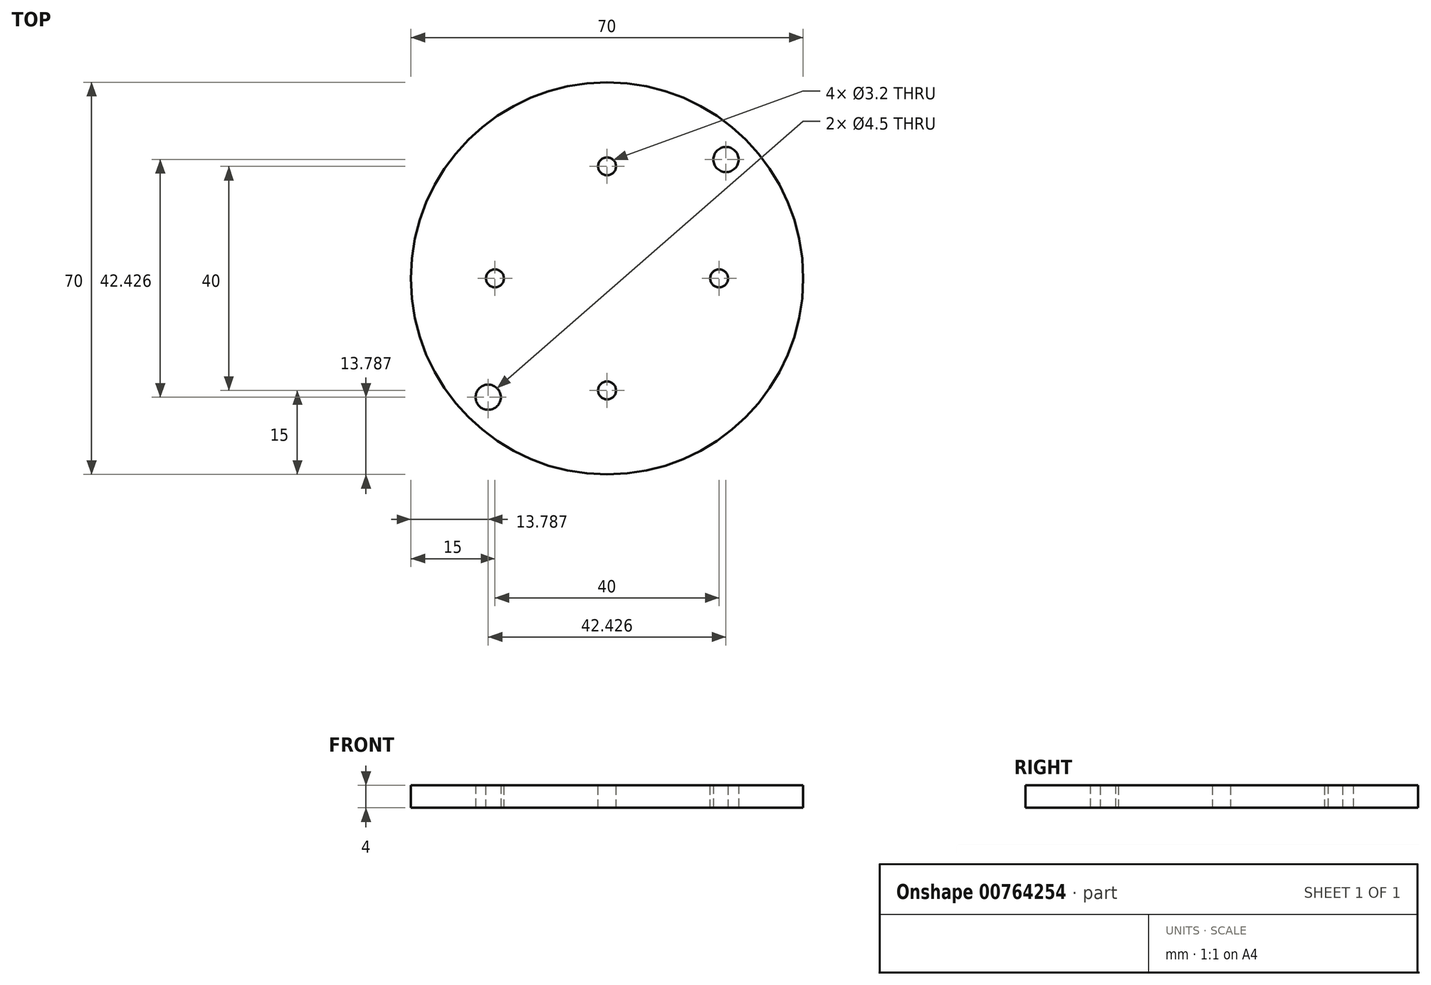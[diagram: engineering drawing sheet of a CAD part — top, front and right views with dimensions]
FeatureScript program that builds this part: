
annotation { "Feature Type Name" : "Feature", "Feature Type Description" : "" }
export const myFeature = defineFeature(function(context is Context, id is Id, definition is map)
    precondition{}
    {
        {
            var Q0;
            Q0=qCreatedBy(makeId("Top.planeOp"),FACE);
            var sketch = newSketch(context, id + "F0", { "sketchPlane" : qUnion([Q0])});
            skCircle(sketch, "E0", {"center": v(0, 0) * mm, "radius": 35 * mm});
            skLineSegment(sketch, "E1", {"start": v(-21.21, -21.21) * mm, "end": v(0, 0) * mm});
            skLineSegment(sketch, "E2", {"start": v(0, 0) * mm, "end": v(21.21, 21.21) * mm});
            skLineSegment(sketch, "E3", {"start": v(21.21, 21.21) * mm, "end": v(0, 0) * mm});
            skCircle(sketch, "E4", {"center": v(21.21, 21.21) * mm, "radius": 2.25 * mm});
            skCircle(sketch, "E5", {"center": v(-21.21, -21.21) * mm, "radius": 2.25 * mm});
            skSolve(sketch);
        }
        {
            var Q0;
            Q0 = qSketchRegion(id + "F0", true);
            extrude(context, id + "F1", {"entities" : qUnion([Q0]), "depth" : 4 * mm, "offsetDistance" : 25 * mm});
        }
        {
            var Q0;
            Q0=makeQuery(id+"F1.opExtrude","CAP_FACE",FACE,{"disambiguationData":[OSD([sQuery(id+"F0.wireOp",EDGE,"E0"),sQuery(id+"F0.wireOp",EDGE,"de1Grw44-cGFu-5i0o-8A4r-Zq54lEinxhuE"),sQuery(id+"F0.wireOp",EDGE,"E4"),sQuery(id+"F0.wireOp",EDGE,"CMPWbkWI-gggi-udjs-4O77-vAyiC2Vh54Nz"),sQuery(id+"F0.wireOp",EDGE,"E5")])],"isStart":false});
            var sketch = newSketch(context, id + "F2", { "sketchPlane" : qUnion([Q0])});
            skCircle(sketch, "E6", {"center": v(0, 0) * mm, "radius": 20 * mm});
            skCircle(sketch, "E7", {"center": v(0, -20) * mm, "radius": 1.6 * mm});
            skCircle(sketch, "E8", {"center": v(20, 0) * mm, "radius": 1.6 * mm});
            skCircle(sketch, "E9", {"center": v(0, 20) * mm, "radius": 1.6 * mm});
            skCircle(sketch, "E10", {"center": v(-20, 0) * mm, "radius": 1.6 * mm});
            skLineSegment(sketch, "E11", {"start": v(0, 0) * mm, "end": v(0, 20) * mm});
            skLineSegment(sketch, "E12", {"start": v(-20, 0) * mm, "end": v(0, 0) * mm});
            skLineSegment(sketch, "E13", {"start": v(0, -20) * mm, "end": v(0, 0) * mm});
            skLineSegment(sketch, "E14", {"start": v(0, 0) * mm, "end": v(20, 0) * mm});
            skSolve(sketch);
        }
        {
            var Q0;
            {var subQ0=sQuery(id+"F2.wireOp",EDGE,"E6");var subQ1=makeQuery(id+"F2.imprint","INTERSECT",VERTEX,{"derivedFrom":[subQ0,sQuery(id+"F2.wireOp",EDGE,"E11")]});Q0=makeQuery(id+"F2.imprint","IMPRINT",FACE,{"disambiguationData":[TD([[makeQuery(id+"F2.imprint","IMPRINT",EDGE,{"disambiguationData":[TD([[subQ1,1.0]])],"derivedFrom":subQ0}),-1.0]])]});}
            var Q1;
            {var subQ0=sQuery(id+"F2.wireOp",EDGE,"E11");var subQ1=sQuery(id+"F2.wireOp",EDGE,"E6");var subQ2=makeQuery(id+"F2.imprint","INTERSECT",VERTEX,{"derivedFrom":[subQ1,subQ0]});Q1=makeQuery(id+"F2.imprint","IMPRINT",FACE,{"disambiguationData":[TD([[makeQuery(id+"F2.imprint","IMPRINT",EDGE,{"disambiguationData":[TD([[subQ2,1.0]])],"derivedFrom":subQ1}),1.0]])]});}
            var Q2;
            {var subQ0=sQuery(id+"F2.wireOp",EDGE,"E11");var subQ1=sQuery(id+"F2.wireOp",EDGE,"E6");var subQ2=makeQuery(id+"F2.imprint","INTERSECT",VERTEX,{"derivedFrom":[subQ1,subQ0]});Q2=makeQuery(id+"F2.imprint","IMPRINT",FACE,{"disambiguationData":[TD([[makeQuery(id+"F2.imprint","IMPRINT",EDGE,{"disambiguationData":[TD([[subQ2,-1.0]])],"derivedFrom":subQ1}),1.0]])]});}
            var Q3;
            {var subQ0=sQuery(id+"F2.wireOp",EDGE,"E6");var subQ1=makeQuery(id+"F2.imprint","INTERSECT",VERTEX,{"derivedFrom":[subQ0,sQuery(id+"F2.wireOp",EDGE,"E12")]});Q3=makeQuery(id+"F2.imprint","IMPRINT",FACE,{"disambiguationData":[TD([[makeQuery(id+"F2.imprint","IMPRINT",EDGE,{"disambiguationData":[TD([[subQ1,1.0]])],"derivedFrom":subQ0}),-1.0]])]});}
            var Q4;
            {var subQ0=sQuery(id+"F2.wireOp",EDGE,"E12");var subQ1=sQuery(id+"F2.wireOp",EDGE,"E6");var subQ2=makeQuery(id+"F2.imprint","INTERSECT",VERTEX,{"derivedFrom":[subQ1,subQ0]});Q4=makeQuery(id+"F2.imprint","IMPRINT",FACE,{"disambiguationData":[TD([[makeQuery(id+"F2.imprint","IMPRINT",EDGE,{"disambiguationData":[TD([[subQ2,1.0]])],"derivedFrom":subQ1}),1.0]])]});}
            var Q5;
            {var subQ0=sQuery(id+"F2.wireOp",EDGE,"E12");var subQ1=sQuery(id+"F2.wireOp",EDGE,"E6");var subQ2=makeQuery(id+"F2.imprint","INTERSECT",VERTEX,{"derivedFrom":[subQ1,subQ0]});Q5=makeQuery(id+"F2.imprint","IMPRINT",FACE,{"disambiguationData":[TD([[makeQuery(id+"F2.imprint","IMPRINT",EDGE,{"disambiguationData":[TD([[subQ2,-1.0]])],"derivedFrom":subQ1}),1.0]])]});}
            var Q6;
            {var subQ0=sQuery(id+"F2.wireOp",EDGE,"E6");var subQ1=makeQuery(id+"F2.imprint","INTERSECT",VERTEX,{"derivedFrom":[subQ0,sQuery(id+"F2.wireOp",EDGE,"E13")]});Q6=makeQuery(id+"F2.imprint","IMPRINT",FACE,{"disambiguationData":[TD([[makeQuery(id+"F2.imprint","IMPRINT",EDGE,{"disambiguationData":[TD([[subQ1,1.0]])],"derivedFrom":subQ0}),-1.0]])]});}
            var Q7;
            {var subQ0=sQuery(id+"F2.wireOp",EDGE,"E13");var subQ1=sQuery(id+"F2.wireOp",EDGE,"E6");var subQ2=makeQuery(id+"F2.imprint","INTERSECT",VERTEX,{"derivedFrom":[subQ1,subQ0]});Q7=makeQuery(id+"F2.imprint","IMPRINT",FACE,{"disambiguationData":[TD([[makeQuery(id+"F2.imprint","IMPRINT",EDGE,{"disambiguationData":[TD([[subQ2,1.0]])],"derivedFrom":subQ1}),1.0]])]});}
            var Q8;
            {var subQ0=sQuery(id+"F2.wireOp",EDGE,"E13");var subQ1=sQuery(id+"F2.wireOp",EDGE,"E6");var subQ2=makeQuery(id+"F2.imprint","INTERSECT",VERTEX,{"derivedFrom":[subQ1,subQ0]});Q8=makeQuery(id+"F2.imprint","IMPRINT",FACE,{"disambiguationData":[TD([[makeQuery(id+"F2.imprint","IMPRINT",EDGE,{"disambiguationData":[TD([[subQ2,-1.0]])],"derivedFrom":subQ1}),1.0]])]});}
            var Q9;
            {var subQ0=sQuery(id+"F2.wireOp",EDGE,"E6");var subQ1=makeQuery(id+"F2.imprint","INTERSECT",VERTEX,{"derivedFrom":[subQ0,sQuery(id+"F2.wireOp",EDGE,"E14")]});Q9=makeQuery(id+"F2.imprint","IMPRINT",FACE,{"disambiguationData":[TD([[makeQuery(id+"F2.imprint","IMPRINT",EDGE,{"disambiguationData":[TD([[subQ1,1.0]])],"derivedFrom":subQ0}),-1.0]])]});}
            var Q10;
            {var subQ0=sQuery(id+"F2.wireOp",EDGE,"E14");var subQ1=sQuery(id+"F2.wireOp",EDGE,"E6");var subQ2=makeQuery(id+"F2.imprint","INTERSECT",VERTEX,{"derivedFrom":[subQ1,subQ0]});Q10=makeQuery(id+"F2.imprint","IMPRINT",FACE,{"disambiguationData":[TD([[makeQuery(id+"F2.imprint","IMPRINT",EDGE,{"disambiguationData":[TD([[subQ2,1.0]])],"derivedFrom":subQ1}),1.0]])]});}
            var Q11;
            {var subQ0=sQuery(id+"F2.wireOp",EDGE,"E14");var subQ1=sQuery(id+"F2.wireOp",EDGE,"E6");var subQ2=makeQuery(id+"F2.imprint","INTERSECT",VERTEX,{"derivedFrom":[subQ1,subQ0]});Q11=makeQuery(id+"F2.imprint","IMPRINT",FACE,{"disambiguationData":[TD([[makeQuery(id+"F2.imprint","IMPRINT",EDGE,{"disambiguationData":[TD([[subQ2,-1.0]])],"derivedFrom":subQ1}),1.0]])]});}
            extrude(context, id + "F3", {"entities" : qUnion([Q0, Q1, Q2, Q3, Q4, Q5, Q6, Q7, Q8, Q9, Q10, Q11]), "operationType" : NewBodyOperationType.REMOVE, "endBound" : BoundingType.THROUGH_ALL, "oppositeDirection" : true, "depth" : 25 * mm, "offsetDistance" : 25 * mm});
        }
    });
